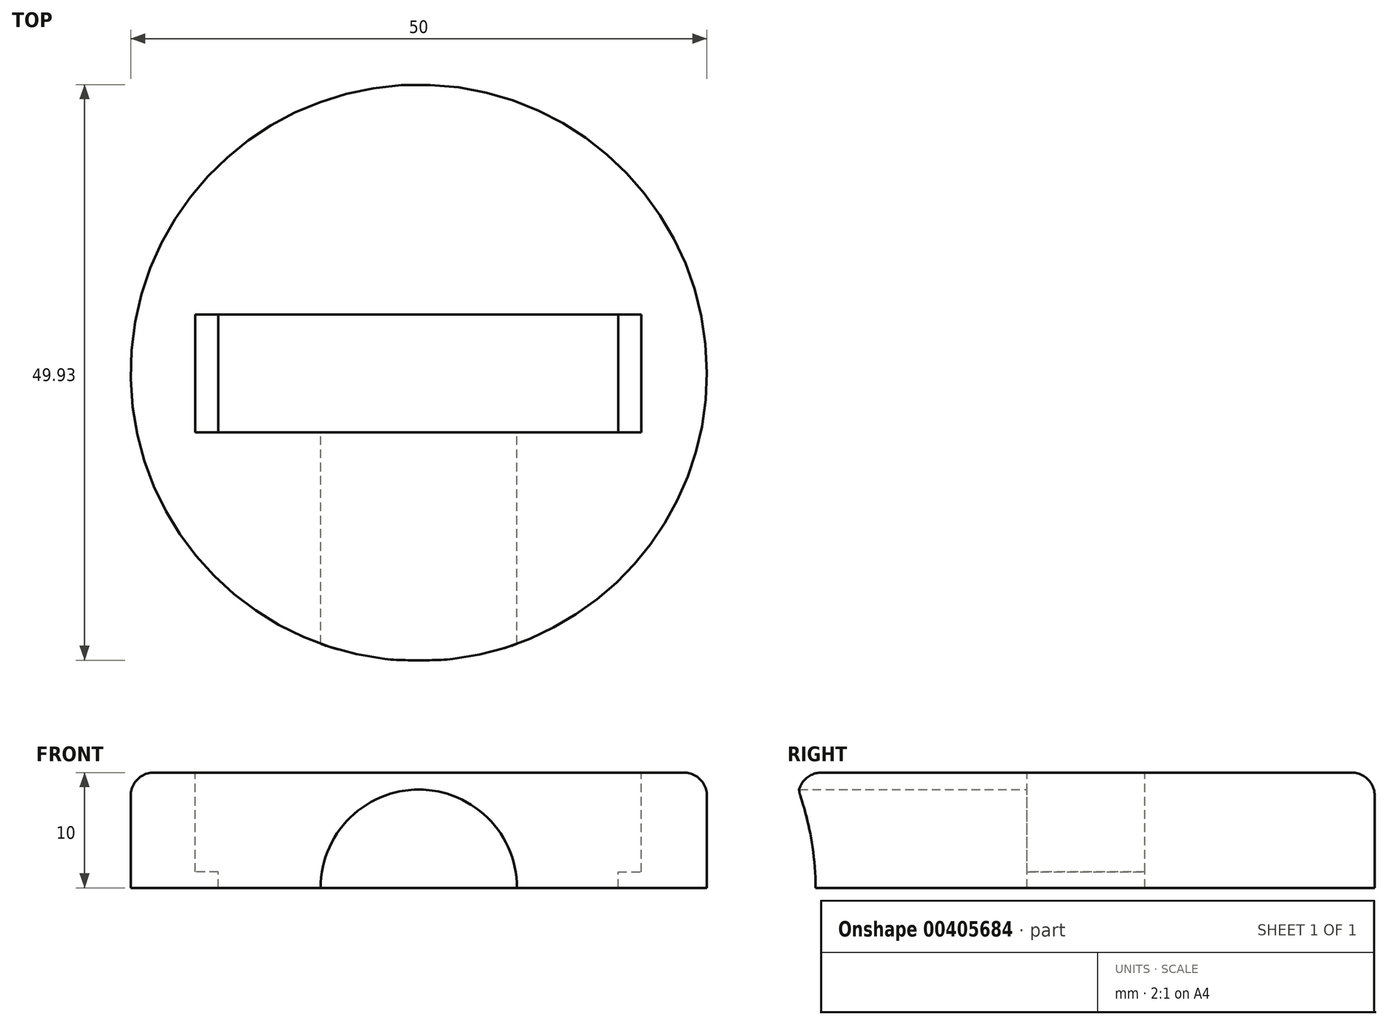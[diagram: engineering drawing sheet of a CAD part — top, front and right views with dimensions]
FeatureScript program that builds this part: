
annotation { "Feature Type Name" : "Feature", "Feature Type Description" : "" }
export const myFeature = defineFeature(function(context is Context, id is Id, definition is map)
    precondition{}
    {
        {
            var Q0;
            Q0=qCreatedBy(makeId("Top.planeOp"),FACE);
            var sketch = newSketch(context, id + "F0", { "sketchPlane" : qUnion([Q0])});
            skCircle(sketch, "E0", {"center": v(0, 0) * mm, "radius": 25 * mm});
            skSolve(sketch);
        }
        {
            var Q0;
            Q0=makeQuery(id+"F0.imprint","IMPRINT",FACE,{"disambiguationData":[TD([[makeQuery(id+"F0.imprint","IMPRINT",EDGE,{"derivedFrom":sQuery(id+"F0.wireOp",EDGE,"E0")}),1.0]])]});
            extrude(context, id + "F1", {"entities" : qUnion([Q0]), "depth" : 10 * mm});
        }
        {
            var Q0;
            Q0=makeQuery(id+"F1.opExtrude","CAP_FACE",FACE,{"disambiguationData":[OSD([sQuery(id+"F0.wireOp",EDGE,"E0")])],"isStart":false});
            var sketch = newSketch(context, id + "F2", { "sketchPlane" : qUnion([Q0])});
            skLineSegment(sketch, "E1.bottom", {"start": v(-19.4, -5.15) * mm, "end": v(19.3, -5.15) * mm});
            skLineSegment(sketch, "E1.top", {"start": v(-19.4, 5.05) * mm, "end": v(19.3, 5.05) * mm});
            skLineSegment(sketch, "E1.left", {"start": v(-19.4, -5.15) * mm, "end": v(-19.4, 5.05) * mm});
            skLineSegment(sketch, "E1.right", {"start": v(19.3, -5.15) * mm, "end": v(19.3, 5.05) * mm});
            skSolve(sketch);
        }
        {
            var Q0;
            Q0=makeQuery(id+"F2.imprint","IMPRINT",FACE,{"disambiguationData":[TD([[makeQuery(id+"F2.imprint","IMPRINT",EDGE,{"derivedFrom":sQuery(id+"F2.wireOp",EDGE,"E1.bottom")}),1.0]])]});
            extrude(context, id + "F3", {"entities" : qUnion([Q0]), "operationType" : NewBodyOperationType.REMOVE, "oppositeDirection" : true, "depth" : 11 * mm});
        }
        {
            var Q0;
            Q0=makeQuery(id+"F3.boolean.opBoolean","COPY",FACE,{"derivedFrom":makeQuery(id+"F3.opExtrude","SWEPT_FACE",FACE,{"disambiguationData":[OSD([sQuery(id+"F2.wireOp",EDGE,"E1.right")])]})});
            var sketch = newSketch(context, id + "F4", { "sketchPlane" : qUnion([Q0])});
            skLineSegment(sketch, "E2", {"start": v(-5.05, 1.4) * mm, "end": v(5.15, 1.4) * mm});
            skLineSegment(sketch, "E3", {"start": v(5.15, 1.4) * mm, "end": v(5.15, 0) * mm});
            skLineSegment(sketch, "E4", {"start": v(5.15, 0) * mm, "end": v(-5.05, 0) * mm});
            skLineSegment(sketch, "E5", {"start": v(-5.05, 0) * mm, "end": v(-5.05, 1.4) * mm});
            skSolve(sketch);
        }
        {
            var Q0;
            Q0 = qSketchRegion(id + "F4", true);
            extrude(context, id + "F5", {"entities" : qUnion([Q0]), "operationType" : NewBodyOperationType.ADD, "depth" : 2 * mm});
        }
        {
            var Q0;
            Q0=makeQuery(id+"F3.boolean.opBoolean","COPY",FACE,{"derivedFrom":makeQuery(id+"F3.opExtrude","SWEPT_FACE",FACE,{"disambiguationData":[OSD([sQuery(id+"F2.wireOp",EDGE,"E1.left")])]})});
            var sketch = newSketch(context, id + "F6", { "sketchPlane" : qUnion([Q0])});
            skLineSegment(sketch, "E6", {"start": v(-5.15, 0) * mm, "end": v(-5.15, 1.4) * mm});
            skLineSegment(sketch, "E7", {"start": v(-5.15, 1.4) * mm, "end": v(5.05, 1.4) * mm});
            skLineSegment(sketch, "E8", {"start": v(5.05, 1.4) * mm, "end": v(5.05, 0) * mm});
            skLineSegment(sketch, "E9", {"start": v(5.05, 0) * mm, "end": v(-5.15, 0) * mm});
            skSolve(sketch);
        }
        {
            var Q0;
            Q0=makeQuery(id+"F6.imprint","IMPRINT",FACE,{"disambiguationData":[TD([[makeQuery(id+"F6.imprint","IMPRINT",EDGE,{"derivedFrom":sQuery(id+"F6.wireOp",EDGE,"E6")}),-1.0]])]});
            extrude(context, id + "F7", {"entities" : qUnion([Q0]), "operationType" : NewBodyOperationType.ADD, "depth" : 2 * mm});
        }
        {
            var Q0;
            Q0=makeQuery(id+"F3.boolean.opBoolean","COPY",FACE,{"derivedFrom":makeQuery(id+"F3.opExtrude","SWEPT_FACE",FACE,{"disambiguationData":[OSD([sQuery(id+"F2.wireOp",EDGE,"E1.bottom")])]})});
            var sketch = newSketch(context, id + "F8", { "sketchPlane" : qUnion([Q0])});
            skCircle(sketch, "E10", {"center": v(0, 0) * mm, "radius": 8.52 * mm});
            skSolve(sketch);
        }
        {
            var Q0;
            {var subQ0=sQuery(id+"F8.wireOp",EDGE,"E10");var subQ1=makeQuery(id+"F3.boolean.opBoolean","INTERSECT",EDGE,{"derivedFrom":[makeQuery(id+"F1.opExtrude","CAP_FACE",FACE,{"disambiguationData":[OSD([sQuery(id+"F0.wireOp",EDGE,"E0")])],"isStart":true}),makeQuery(id+"F3.opExtrude","SWEPT_FACE",FACE,{"disambiguationData":[OSD([sQuery(id+"F2.wireOp",EDGE,"E1.bottom")])]})]});var subQ2=makeQuery(id+"F8.imprint","INTERSECT",VERTEX,{"disambiguationData":[OD(0.0)],"derivedFrom":[subQ1,subQ0]});Q0=makeQuery(id+"F8.imprint","IMPRINT",FACE,{"disambiguationData":[TD([[makeQuery(id+"F8.imprint","IMPRINT",EDGE,{"disambiguationData":[TD([[subQ2,1.0]])],"derivedFrom":subQ0}),1.0]])]});}
            extrude(context, id + "F9", {"entities" : qUnion([Q0]), "operationType" : NewBodyOperationType.REMOVE, "oppositeDirection" : true, "depth" : 25 * mm});
        }
        {
            var Q0;
            Q0=makeQuery(id+"F1.opExtrude","CAP_EDGE",EDGE,{"disambiguationData":[OSD([sQuery(id+"F0.wireOp",EDGE,"E0")])],"isStart":false});
            fillet(context, id + "F10", {"entities" : qUnion([Q0]), "radius" : 2 * mm, "tangentPropagation" : true, "allowEdgeOverflow" : false});
        }
    });
